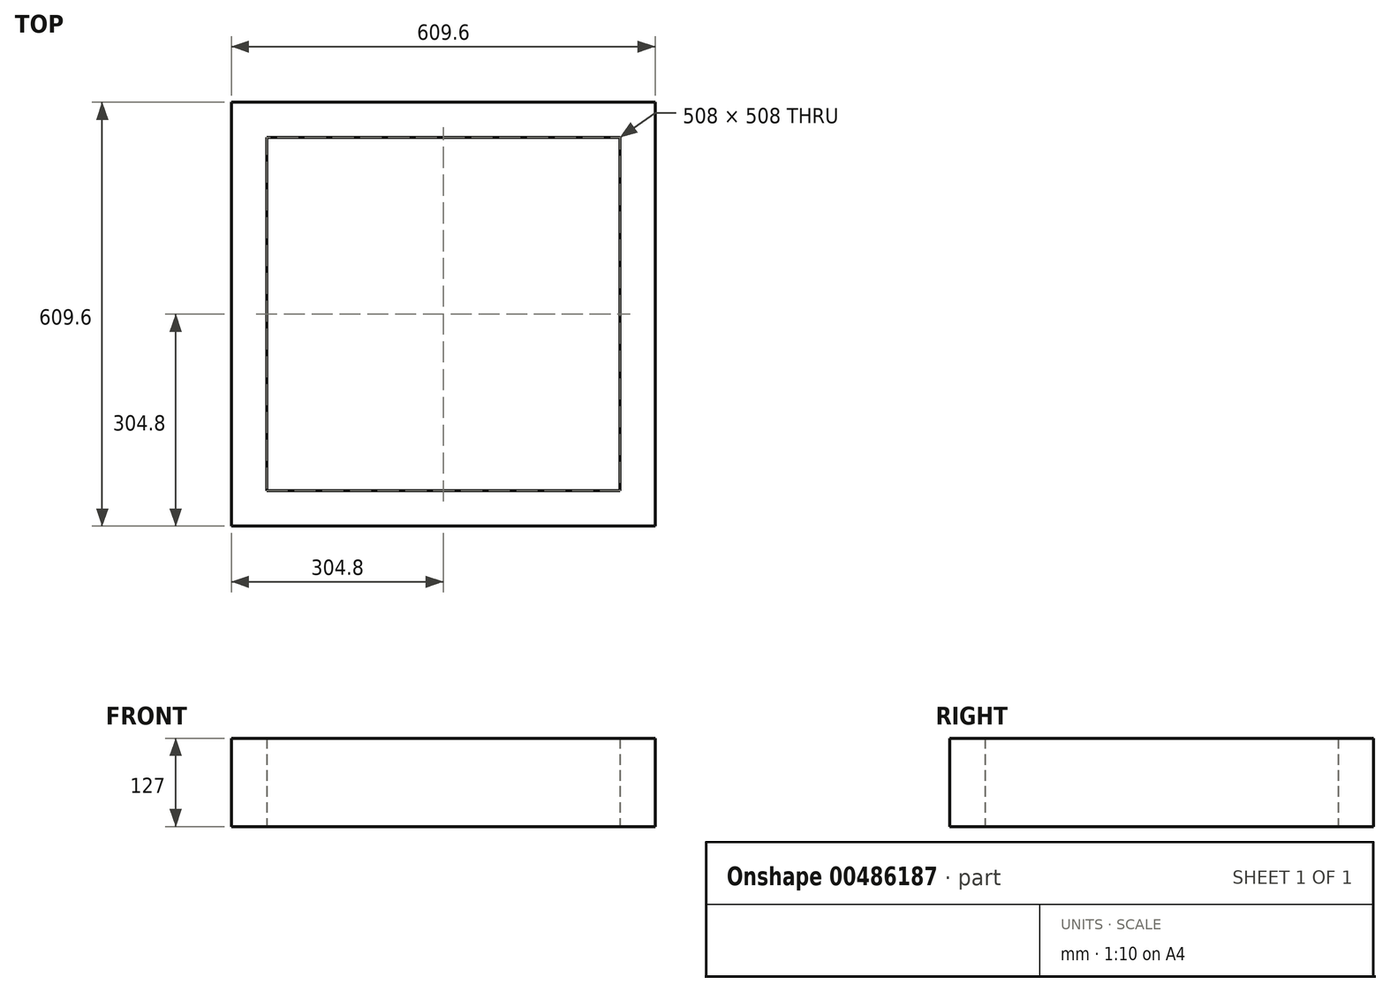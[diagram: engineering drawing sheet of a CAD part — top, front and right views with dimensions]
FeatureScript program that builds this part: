
annotation { "Feature Type Name" : "Feature", "Feature Type Description" : "" }
export const myFeature = defineFeature(function(context is Context, id is Id, definition is map)
    precondition{}
    {
        {
            var Q0;
            Q0=qCreatedBy(makeId("Top.planeOp"),FACE);
            var sketch = newSketch(context, id + "F0", { "sketchPlane" : qUnion([Q0])});
            skLineSegment(sketch, "E0.bottom", {"start": v(304.8, -304.8) * mm, "end": v(-304.8, -304.8) * mm});
            skLineSegment(sketch, "E0.top", {"start": v(304.8, 304.8) * mm, "end": v(-304.8, 304.8) * mm});
            skLineSegment(sketch, "E0.left", {"start": v(304.8, -304.8) * mm, "end": v(304.8, 304.8) * mm});
            skLineSegment(sketch, "E0.right", {"start": v(-304.8, -304.8) * mm, "end": v(-304.8, 304.8) * mm});
            skPoint(sketch, "E0.middle", {"position": v(0, 0) * mm});
            skLineSegment(sketch, "E1.bottom", {"start": v(254, -254) * mm, "end": v(-254, -254) * mm});
            skLineSegment(sketch, "E1.top", {"start": v(254, 254) * mm, "end": v(-254, 254) * mm});
            skLineSegment(sketch, "E1.left", {"start": v(254, -254) * mm, "end": v(254, 254) * mm});
            skLineSegment(sketch, "E1.right", {"start": v(-254, -254) * mm, "end": v(-254, 254) * mm});
            skSolve(sketch);
        }
        {
            var Q0;
            Q0 = qSketchRegion(id + "F0", true);
            extrude(context, id + "F1", {"entities" : qUnion([Q0]), "depth" : 127 * mm});
        }
    });
